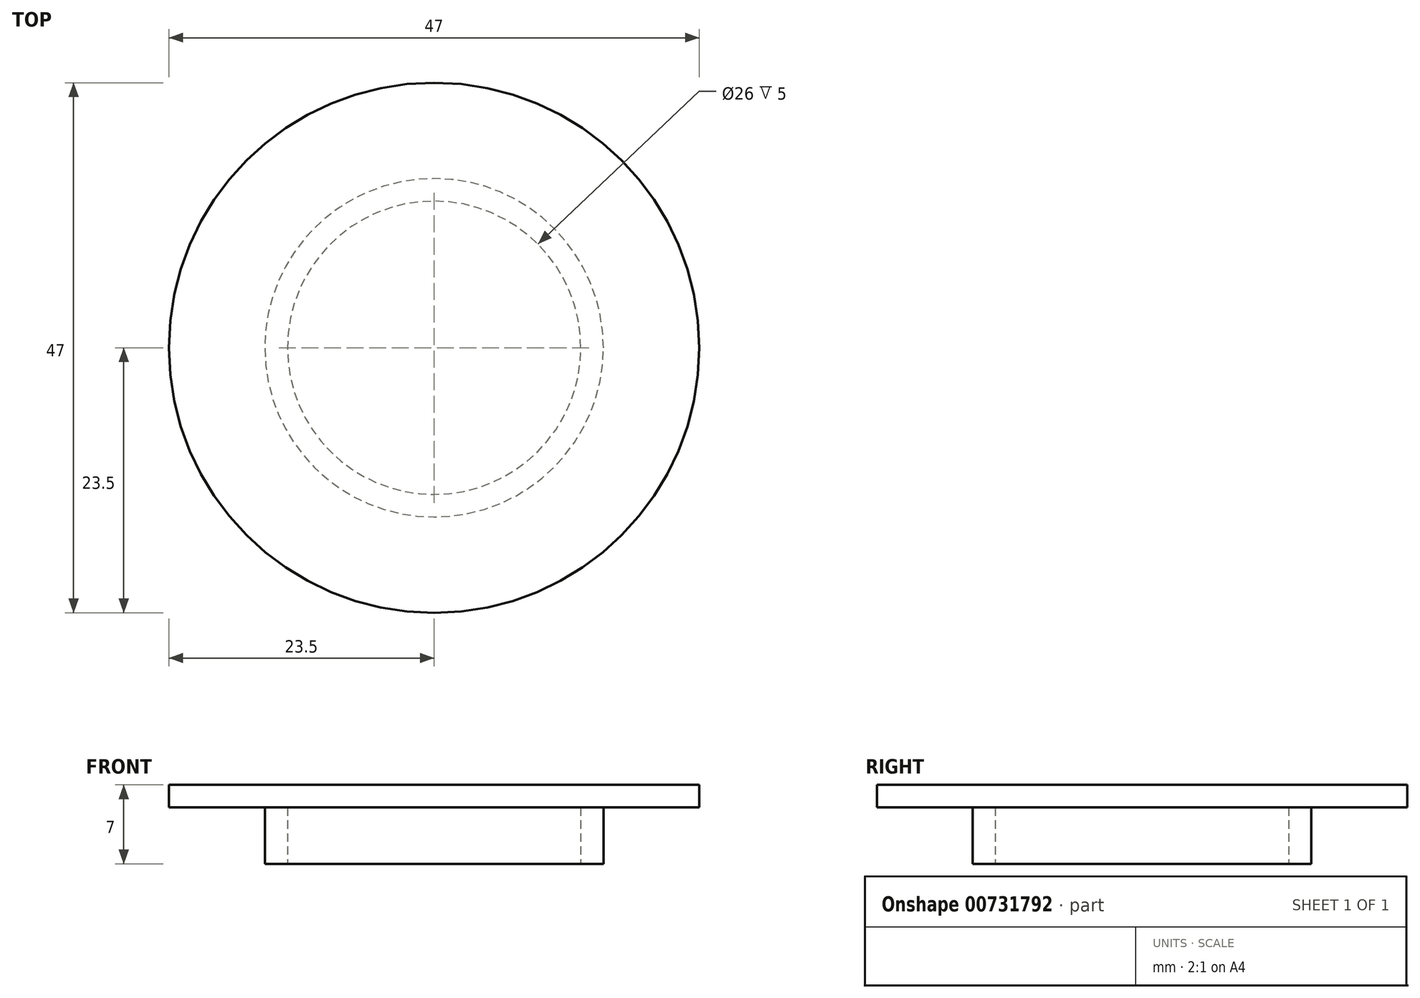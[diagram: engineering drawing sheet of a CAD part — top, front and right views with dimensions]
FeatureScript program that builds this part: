
annotation { "Feature Type Name" : "Feature", "Feature Type Description" : "" }
export const myFeature = defineFeature(function(context is Context, id is Id, definition is map)
    precondition{}
    {
        {
            var Q0;
            Q0=qCreatedBy(makeId("Front.planeOp"),FACE);
            var sketch = newSketch(context, id + "F0", { "sketchPlane" : qUnion([Q0])});
            skLineSegment(sketch, "E0", {"start": v(0, 0) * mm, "end": v(0, 2) * mm});
            skLineSegment(sketch, "E1", {"start": v(0, 2) * mm, "end": v(-23.5, 2) * mm});
            skLineSegment(sketch, "E2", {"start": v(-23.5, 2) * mm, "end": v(-23.5, 0) * mm});
            skLineSegment(sketch, "E3", {"start": v(-23.5, 0) * mm, "end": v(-15, 0) * mm});
            skLineSegment(sketch, "E4", {"start": v(-15, 0) * mm, "end": v(-15, -5) * mm});
            skLineSegment(sketch, "E5", {"start": v(-15, -5) * mm, "end": v(-13, -5) * mm});
            skLineSegment(sketch, "E6", {"start": v(-13, -5) * mm, "end": v(-13, 0) * mm});
            skLineSegment(sketch, "E7", {"start": v(-13, 0) * mm, "end": v(0, 0) * mm});
            skSolve(sketch);
        }
        {
            var Q0;
            Q0=makeQuery(id+"F0.imprint","IMPRINT",FACE,{"disambiguationData":[TD([[makeQuery(id+"F0.imprint","IMPRINT",EDGE,{"derivedFrom":sQuery(id+"F0.wireOp",EDGE,"E0")}),1.0]])]});
            var Q1;
            Q1=sQuery(id+"F0.wireOp",EDGE,"E0");
            revolve(context, id + "F1", {"surfaceOperationType" : NewSurfaceOperationType.NEW, "entities" : qUnion([Q0]), "axis" : qUnion([Q1]), "revolveType" : RevolveType.FULL});
        }
    });
